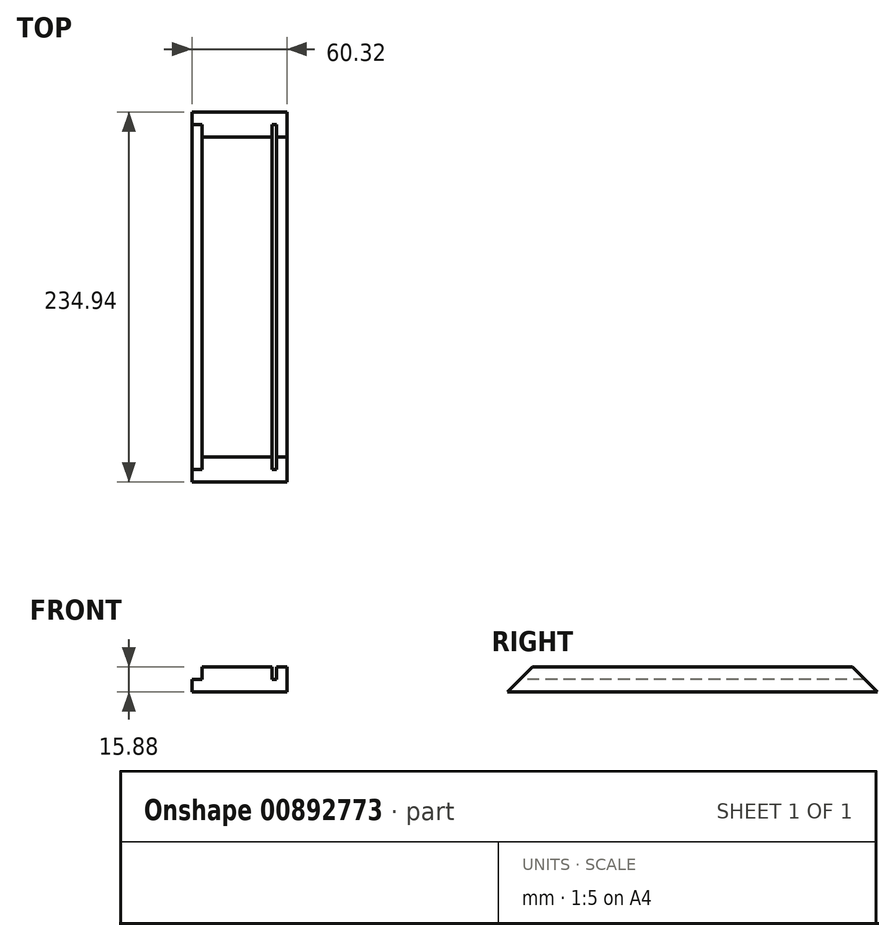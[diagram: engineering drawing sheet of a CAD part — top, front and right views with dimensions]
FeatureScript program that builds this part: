
annotation { "Feature Type Name" : "Feature", "Feature Type Description" : "" }
export const myFeature = defineFeature(function(context is Context, id is Id, definition is map)
    precondition{}
    {
        {
            var Q0;
            Q0=qCreatedBy(makeId("Right.planeOp"),FACE);
            var sketch = newSketch(context, id + "F0", { "sketchPlane" : qUnion([Q0])});
            skLineSegment(sketch, "E0.bottom", {"start": v(117.48, 7.94) * mm, "end": v(-117.48, 7.94) * mm});
            skLineSegment(sketch, "E0.top", {"start": v(117.48, -7.94) * mm, "end": v(-117.48, -7.94) * mm});
            skLineSegment(sketch, "E0.left", {"start": v(117.48, 7.94) * mm, "end": v(117.48, -7.94) * mm});
            skLineSegment(sketch, "E0.right", {"start": v(-117.48, 7.94) * mm, "end": v(-117.48, -7.94) * mm});
            skPoint(sketch, "E0.middle", {"position": v(0, 0) * mm});
            skSolve(sketch);
        }
        {
            var Q0;
            Q0 = qSketchRegion(id + "F0", true);
            extrude(context, id + "F1", {"entities" : qUnion([Q0]), "depth" : 60.32 * mm, "offsetDistance" : 25.4 * mm});
        }
        {
            var Q0;
            Q0=makeQuery(id+"F1.opExtrude","SWEPT_FACE",FACE,{"disambiguationData":[OSD([sQuery(id+"F0.wireOp",EDGE,"E0.right")])]});
            var sketch = newSketch(context, id + "F2", { "sketchPlane" : qUnion([Q0])});
            skLineSegment(sketch, "E1.bottom", {"start": v(0, 0) * mm, "end": v(6.35, 0) * mm});
            skLineSegment(sketch, "E1.top", {"start": v(0, 7.94) * mm, "end": v(6.35, 7.94) * mm});
            skLineSegment(sketch, "E1.left", {"start": v(0, 0) * mm, "end": v(0, 7.94) * mm});
            skLineSegment(sketch, "E1.right", {"start": v(6.35, 0) * mm, "end": v(6.35, 7.94) * mm});
            skLineSegment(sketch, "E2.bottom", {"start": v(53.8, 7.94) * mm, "end": v(50.8, 7.94) * mm});
            skLineSegment(sketch, "E2.top", {"start": v(53.8, 0) * mm, "end": v(50.8, 0) * mm});
            skLineSegment(sketch, "E2.left", {"start": v(53.8, 7.94) * mm, "end": v(53.8, 0) * mm});
            skLineSegment(sketch, "E2.right", {"start": v(50.8, 7.94) * mm, "end": v(50.8, 0) * mm});
            skSolve(sketch);
        }
        {
            var Q0;
            Q0 = qSketchRegion(id + "F2", true);
            extrude(context, id + "F3", {"entities" : qUnion([Q0]), "operationType" : NewBodyOperationType.REMOVE, "endBound" : BoundingType.THROUGH_ALL, "oppositeDirection" : true, "depth" : 25.4 * mm, "offsetDistance" : 25.4 * mm});
        }
        {
            var Q0;
            Q0=makeQuery(id+"F1.opExtrude","CAP_FACE",FACE,{"disambiguationData":[OSD([sQuery(id+"F0.wireOp",EDGE,"E0.bottom"),sQuery(id+"F0.wireOp",EDGE,"E0.top"),sQuery(id+"F0.wireOp",EDGE,"E0.left"),sQuery(id+"F0.wireOp",EDGE,"E0.right")])],"isStart":false});
            var sketch = newSketch(context, id + "F4", { "sketchPlane" : qUnion([Q0])});
            skLineSegment(sketch, "E3", {"start": v(-117.48, -7.94) * mm, "end": v(-101.6, 7.94) * mm});
            skLineSegment(sketch, "E4.MirrorCS", {"start": v(117.48, -7.94) * mm, "end": v(101.6, 7.94) * mm});
            skSolve(sketch);
        }
        {
            var Q0;
            Q0 = qSketchRegion(id + "F4", true);
            var Q1;
            {var subQ0=sQuery(id+"F4.wireOp",EDGE,"E3");Q1=makeQuery(id+"F4.imprint","IMPRINT",FACE,{"disambiguationData":[TD([[makeQuery(id+"F4.imprint","IMPRINT",EDGE,{"derivedFrom":subQ0}),1.0]])]});}
            var Q2;
            {var subQ0=sQuery(id+"F4.wireOp",EDGE,"E4.MirrorCS");Q2=makeQuery(id+"F4.imprint","IMPRINT",FACE,{"disambiguationData":[TD([[makeQuery(id+"F4.imprint","IMPRINT",EDGE,{"derivedFrom":subQ0}),-1.0]])]});}
            extrude(context, id + "F5", {"entities" : qUnion([Q0, Q1, Q2]), "operationType" : NewBodyOperationType.REMOVE, "endBound" : BoundingType.THROUGH_ALL, "oppositeDirection" : true, "depth" : 25.4 * mm, "offsetDistance" : 25.4 * mm});
        }
    });
